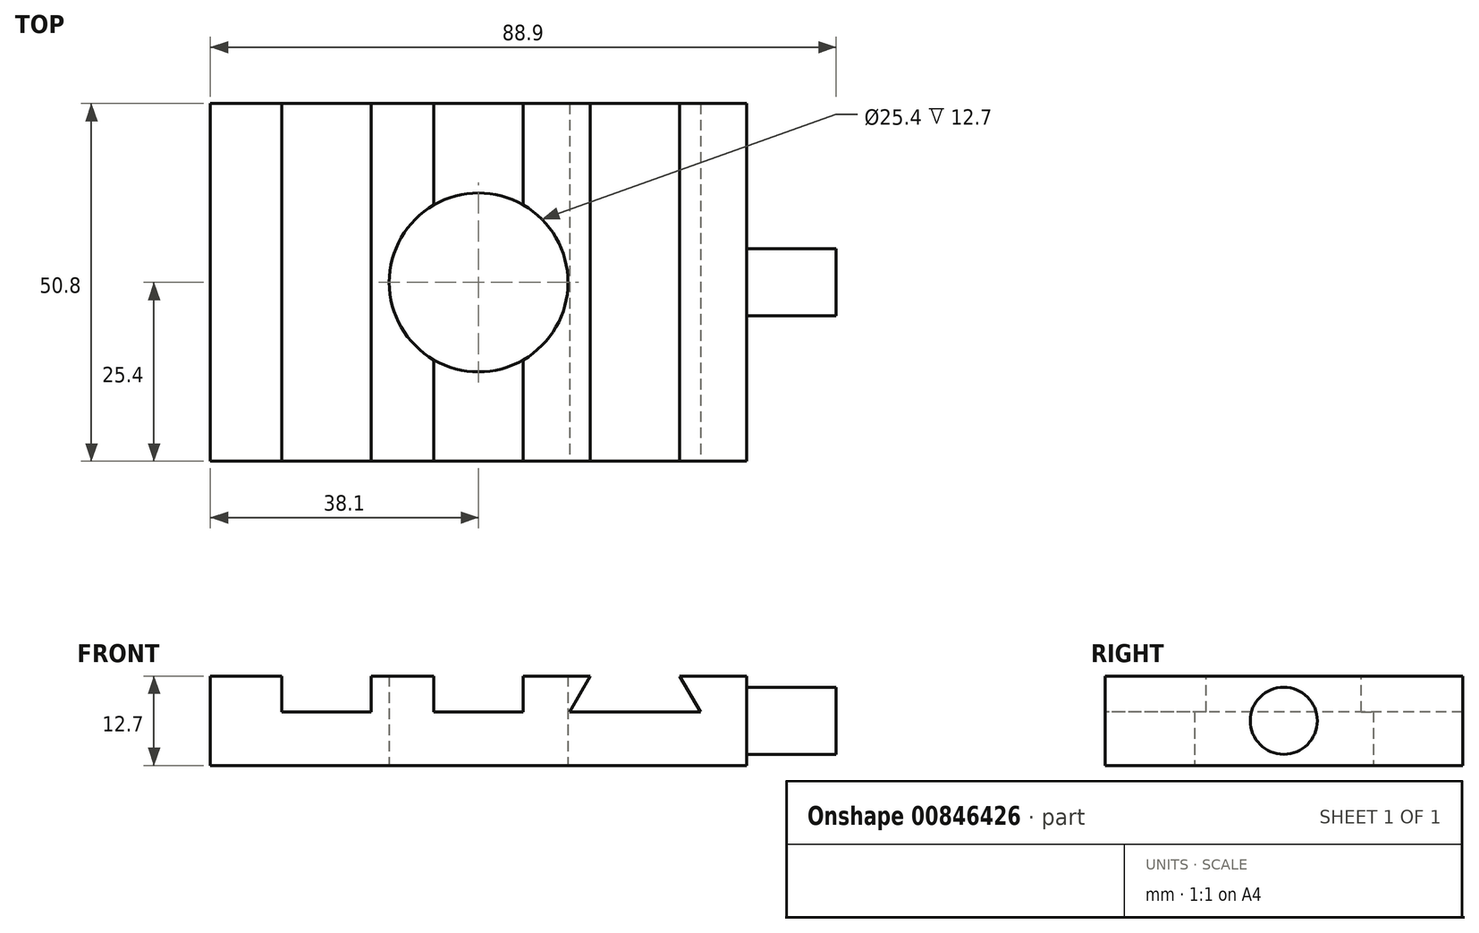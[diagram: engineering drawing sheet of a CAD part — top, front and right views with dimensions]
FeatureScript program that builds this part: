
annotation { "Feature Type Name" : "Feature", "Feature Type Description" : "" }
export const myFeature = defineFeature(function(context is Context, id is Id, definition is map)
    precondition{}
    {
        {
            var Q0;
            Q0=qCreatedBy(makeId("Top.planeOp"),FACE);
            var sketch = newSketch(context, id + "F0", { "sketchPlane" : qUnion([Q0])});
            skLineSegment(sketch, "E0.bottom", {"start": v(38.1, -25.4) * mm, "end": v(-38.1, -25.4) * mm});
            skLineSegment(sketch, "E0.top", {"start": v(38.1, 25.4) * mm, "end": v(-38.1, 25.4) * mm});
            skLineSegment(sketch, "E0.left", {"start": v(38.1, -25.4) * mm, "end": v(38.1, 25.4) * mm});
            skLineSegment(sketch, "E0.right", {"start": v(-38.1, -25.4) * mm, "end": v(-38.1, 25.4) * mm});
            skPoint(sketch, "E0.middle", {"position": v(0, 0) * mm});
            skCircle(sketch, "E1", {"center": v(0, 0) * mm, "radius": 12.7 * mm});
            skSolve(sketch);
        }
        {
            var Q0;
            Q0=makeQuery(id+"F0.imprint","IMPRINT",FACE,{"disambiguationData":[TD([[makeQuery(id+"F0.imprint","IMPRINT",EDGE,{"derivedFrom":sQuery(id+"F0.wireOp",EDGE,"E0.bottom")}),-1.0]])]});
            extrude(context, id + "F1", {"entities" : qUnion([Q0]), "depth" : 12.7 * mm, "offsetDistance" : 25.4 * mm});
        }
        {
            var Q0;
            Q0=makeQuery(id+"F1.opExtrude","CAP_FACE",FACE,{"disambiguationData":[OSD([sQuery(id+"F0.wireOp",EDGE,"E0.bottom"),sQuery(id+"F0.wireOp",EDGE,"E0.top"),sQuery(id+"F0.wireOp",EDGE,"E0.left"),sQuery(id+"F0.wireOp",EDGE,"E0.right"),sQuery(id+"F0.wireOp",EDGE,"E1")])],"isStart":false});
            var sketch = newSketch(context, id + "F2", { "sketchPlane" : qUnion([Q0])});
            skLineSegment(sketch, "E2.bottom", {"start": v(-27.94, 25.4) * mm, "end": v(-15.24, 25.4) * mm});
            skLineSegment(sketch, "E2.top", {"start": v(-27.94, -25.4) * mm, "end": v(-15.24, -25.4) * mm});
            skLineSegment(sketch, "E2.left", {"start": v(-27.94, 25.4) * mm, "end": v(-27.94, -25.4) * mm});
            skLineSegment(sketch, "E2.right", {"start": v(-15.24, 25.4) * mm, "end": v(-15.24, -25.4) * mm});
            skLineSegment(sketch, "E3", {"start": v(-6.35, 25.4) * mm, "end": v(-6.35, -25.4) * mm});
            skLineSegment(sketch, "E4", {"start": v(-6.35, -25.4) * mm, "end": v(6.35, -25.4) * mm});
            skLineSegment(sketch, "E5", {"start": v(6.35, -25.4) * mm, "end": v(6.35, 25.4) * mm});
            skLineSegment(sketch, "E6", {"start": v(6.35, 25.4) * mm, "end": v(-6.35, 25.4) * mm});
            skPoint(sketch, "E7", {"position": v(0, 0) * mm});
            skLineSegment(sketch, "E8", {"start": v(0, 25.4) * mm, "end": v(0, -25.4) * mm, "construction": true});
            skSolve(sketch);
        }
        {
            var Q0;
            Q0=makeQuery(id+"F2.imprint","IMPRINT",FACE,{"disambiguationData":[TD([[makeQuery(id+"F2.imprint","IMPRINT",EDGE,{"derivedFrom":sQuery(id+"F2.wireOp",EDGE,"E2.bottom")}),1.0]])]});
            var Q1;
            {var subQ0=sQuery(id+"F2.wireOp",EDGE,"E4");Q1=makeQuery(id+"F2.imprint","IMPRINT",FACE,{"disambiguationData":[TD([[makeQuery(id+"F2.imprint","IMPRINT",EDGE,{"derivedFrom":subQ0}),-1.0]])]});}
            var Q2;
            {var subQ0=sQuery(id+"F2.wireOp",EDGE,"E6");Q2=makeQuery(id+"F2.imprint","IMPRINT",FACE,{"disambiguationData":[TD([[makeQuery(id+"F2.imprint","IMPRINT",EDGE,{"derivedFrom":subQ0}),1.0]])]});}
            extrude(context, id + "F3", {"entities" : qUnion([Q0, Q1, Q2]), "operationType" : NewBodyOperationType.REMOVE, "oppositeDirection" : true, "depth" : 5.08 * mm, "offsetDistance" : 25.4 * mm});
        }
        {
            var Q0;
            Q0=makeQuery(id+"F1.opExtrude","SWEPT_FACE",FACE,{"disambiguationData":[OSD([sQuery(id+"F0.wireOp",EDGE,"E0.bottom")])]});
            var sketch = newSketch(context, id + "F4", { "sketchPlane" : qUnion([Q0])});
            skLineSegment(sketch, "E9", {"start": v(15.88, 12.7) * mm, "end": v(12.94, 7.62) * mm});
            skLineSegment(sketch, "E10", {"start": v(12.94, 7.62) * mm, "end": v(31.5, 7.62) * mm});
            skLineSegment(sketch, "E11", {"start": v(31.5, 7.62) * mm, "end": v(28.57, 12.7) * mm});
            skLineSegment(sketch, "E12", {"start": v(28.57, 12.7) * mm, "end": v(15.88, 12.7) * mm});
            skLineSegment(sketch, "E13", {"start": v(22.23, 7.62) * mm, "end": v(22.23, 12.7) * mm, "construction": true});
            skPoint(sketch, "E14", {"position": v(22.23, 12.7) * mm});
            skSolve(sketch);
        }
        {
            var Q0;
            Q0=makeQuery(id+"F4.imprint","IMPRINT",FACE,{"disambiguationData":[TD([[makeQuery(id+"F4.imprint","IMPRINT",EDGE,{"derivedFrom":sQuery(id+"F4.wireOp",EDGE,"E9")}),1.0]])]});
            extrude(context, id + "F5", {"entities" : qUnion([Q0]), "operationType" : NewBodyOperationType.REMOVE, "endBound" : BoundingType.THROUGH_ALL, "oppositeDirection" : true, "depth" : 50.8 * mm, "offsetDistance" : 25.4 * mm});
        }
        {
            var Q0;
            Q0=makeQuery(id+"F1.opExtrude","SWEPT_FACE",FACE,{"disambiguationData":[OSD([sQuery(id+"F0.wireOp",EDGE,"E0.left")])]});
            var sketch = newSketch(context, id + "F6", { "sketchPlane" : qUnion([Q0])});
            skCircle(sketch, "E15", {"center": v(0, 6.35) * mm, "radius": 4.76 * mm});
            skPoint(sketch, "E15.centerSnap0", {"position": v(-25.4, 6.35) * mm});
            skPoint(sketch, "E15.centerSnap1", {"position": v(0, 12.7) * mm});
            skSolve(sketch);
        }
        {
            var Q0;
            Q0 = qSketchRegion(id + "F6", true);
            extrude(context, id + "F7", {"entities" : qUnion([Q0]), "operationType" : NewBodyOperationType.ADD, "depth" : 12.7 * mm, "offsetDistance" : 25.4 * mm});
        }
    });
